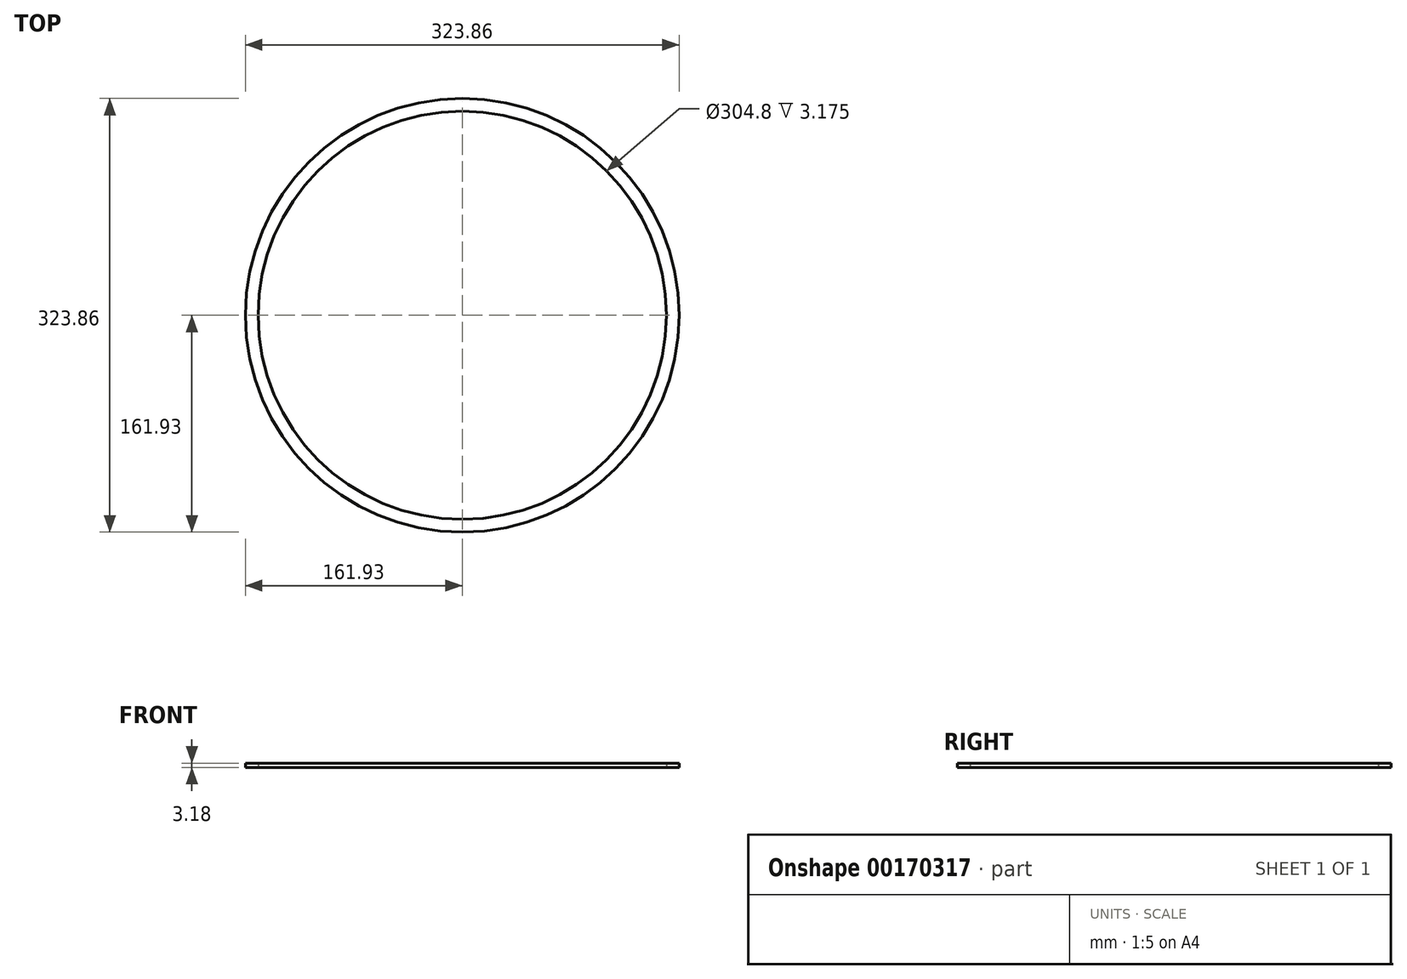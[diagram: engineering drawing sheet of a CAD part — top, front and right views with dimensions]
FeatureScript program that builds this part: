
annotation { "Feature Type Name" : "Feature", "Feature Type Description" : "" }
export const myFeature = defineFeature(function(context is Context, id is Id, definition is map)
    precondition{}
    {
        {
            var Q0;
            Q0=qCreatedBy(makeId("Top.planeOp"),FACE);
            var sketch = newSketch(context, id + "F0", { "sketchPlane" : qUnion([Q0])});
            skCircle(sketch, "E0", {"center": v(0, 0) * mm, "radius": 161.93 * mm});
            skCircle(sketch, "E1", {"center": v(0, 0) * mm, "radius": 152.4 * mm});
            skSolve(sketch);
        }
        {
            var Q0;
            Q0 = qSketchRegion(id + "F0", true);
            extrude(context, id + "F1", {"entities" : qUnion([Q0]), "depth" : 3.17 * mm});
        }
    });
